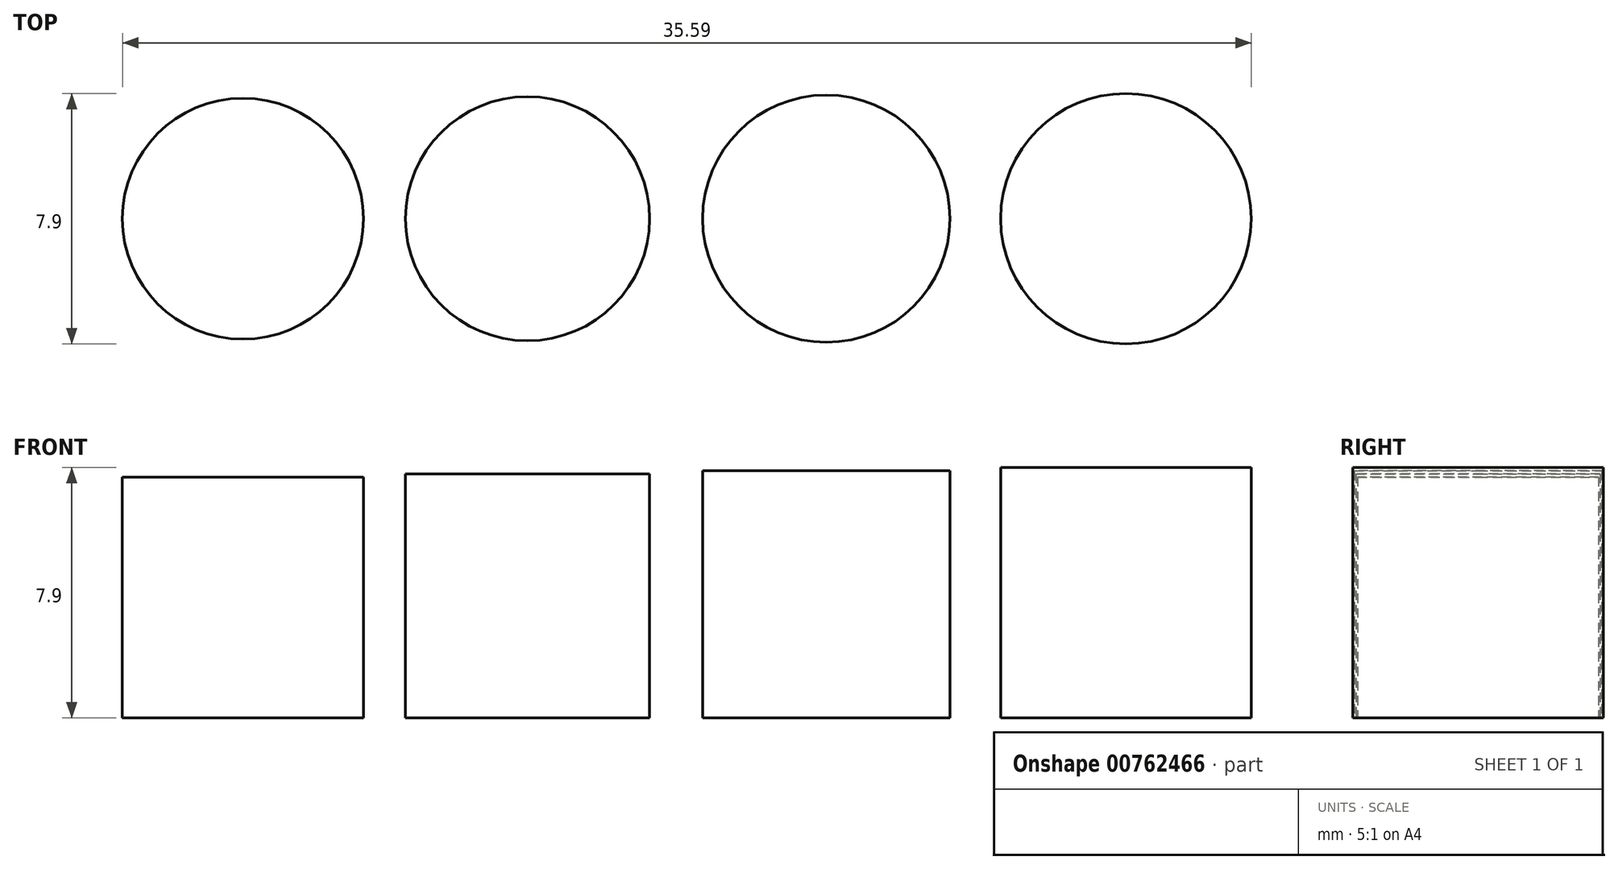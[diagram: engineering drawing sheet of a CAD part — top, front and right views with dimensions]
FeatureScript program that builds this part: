
annotation { "Feature Type Name" : "Feature", "Feature Type Description" : "" }
export const myFeature = defineFeature(function(context is Context, id is Id, definition is map)
    precondition{}
    {
        {
            var Q0;
            Q0=qCreatedBy(makeId("Top.planeOp"),FACE);
            var sketch = newSketch(context, id + "F0", { "sketchPlane" : qUnion([Q0])});
            skCircle(sketch, "E0", {"center": v(0, 0) * mm, "radius": 3.9 * mm});
            skCircle(sketch, "E1", {"center": v(9.45, 0) * mm, "radius": 3.95 * mm});
            skCircle(sketch, "E2", {"center": v(-18.4, 0) * mm, "radius": 3.8 * mm});
            skCircle(sketch, "E3", {"center": v(-9.42, 0) * mm, "radius": 3.85 * mm});
            skSolve(sketch);
        }
        {
            var Q0;
            Q0=makeQuery(id+"F0.imprint","IMPRINT",FACE,{"disambiguationData":[TD([[makeQuery(id+"F0.imprint","IMPRINT",EDGE,{"derivedFrom":sQuery(id+"F0.wireOp",EDGE,"E1")}),1.0]])]});
            extrude(context, id + "F1", {"entities" : qUnion([Q0]), "depth" : 7.9 * mm, "offsetDistance" : 25 * mm});
        }
        {
            var Q0;
            Q0=makeQuery(id+"F0.imprint","IMPRINT",FACE,{"disambiguationData":[TD([[makeQuery(id+"F0.imprint","IMPRINT",EDGE,{"derivedFrom":sQuery(id+"F0.wireOp",EDGE,"E0")}),1.0]])]});
            extrude(context, id + "F2", {"entities" : qUnion([Q0]), "depth" : 7.8 * mm, "offsetDistance" : 25 * mm});
        }
        {
            var Q0;
            Q0=makeQuery(id+"F0.imprint","IMPRINT",FACE,{"disambiguationData":[TD([[makeQuery(id+"F0.imprint","IMPRINT",EDGE,{"derivedFrom":sQuery(id+"F0.wireOp",EDGE,"E3")}),1.0]])]});
            extrude(context, id + "F3", {"entities" : qUnion([Q0]), "depth" : 7.7 * mm, "offsetDistance" : 25 * mm});
        }
        {
            var Q0;
            Q0=makeQuery(id+"F0.imprint","IMPRINT",FACE,{"disambiguationData":[TD([[makeQuery(id+"F0.imprint","IMPRINT",EDGE,{"derivedFrom":sQuery(id+"F0.wireOp",EDGE,"E2")}),1.0]])]});
            extrude(context, id + "F4", {"entities" : qUnion([Q0]), "depth" : 7.6 * mm, "offsetDistance" : 25 * mm});
        }
    });
